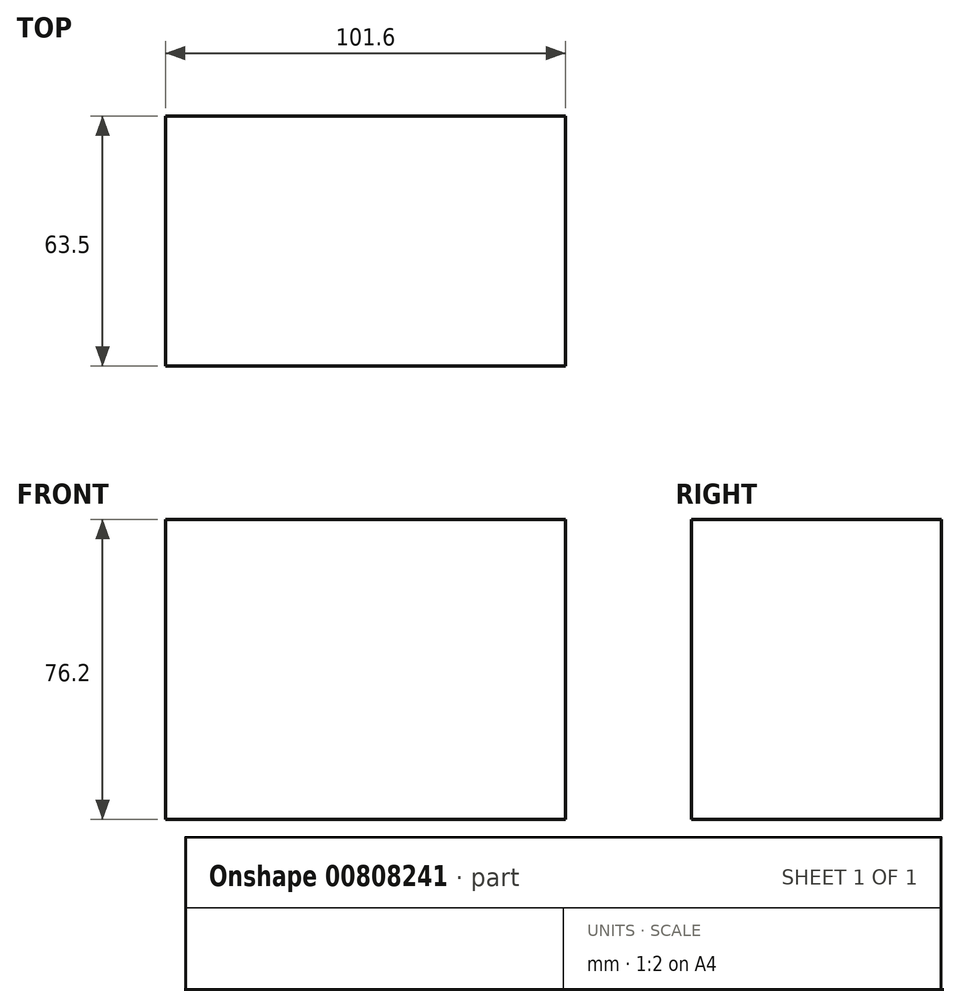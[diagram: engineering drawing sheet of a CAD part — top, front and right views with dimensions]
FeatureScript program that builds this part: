
annotation { "Feature Type Name" : "Feature", "Feature Type Description" : "" }
export const myFeature = defineFeature(function(context is Context, id is Id, definition is map)
    precondition{}
    {
        {
            var Q0;
            Q0=qCreatedBy(makeId("Front.planeOp"),FACE);
            var sketch = newSketch(context, id + "F0", { "sketchPlane" : qUnion([Q0])});
            skLineSegment(sketch, "E0", {"start": v(0, 0) * mm, "end": v(101.6, 0) * mm});
            skLineSegment(sketch, "E1", {"start": v(101.6, 0) * mm, "end": v(101.6, 76.2) * mm});
            skLineSegment(sketch, "E2", {"start": v(101.6, 76.2) * mm, "end": v(0, 76.2) * mm});
            skLineSegment(sketch, "E3", {"start": v(0, 76.2) * mm, "end": v(0, 0) * mm});
            skSolve(sketch);
        }
        {
            var Q0;
            Q0=makeQuery(id+"F0.imprint","IMPRINT",FACE,{"disambiguationData":[TD([[makeQuery(id+"F0.imprint","IMPRINT",EDGE,{"derivedFrom":sQuery(id+"F0.wireOp",EDGE,"E0")}),1.0]])]});
            extrude(context, id + "F1", {"entities" : qUnion([Q0]), "depth" : 63.5 * mm, "offsetDistance" : 25.4 * mm});
        }
    });
